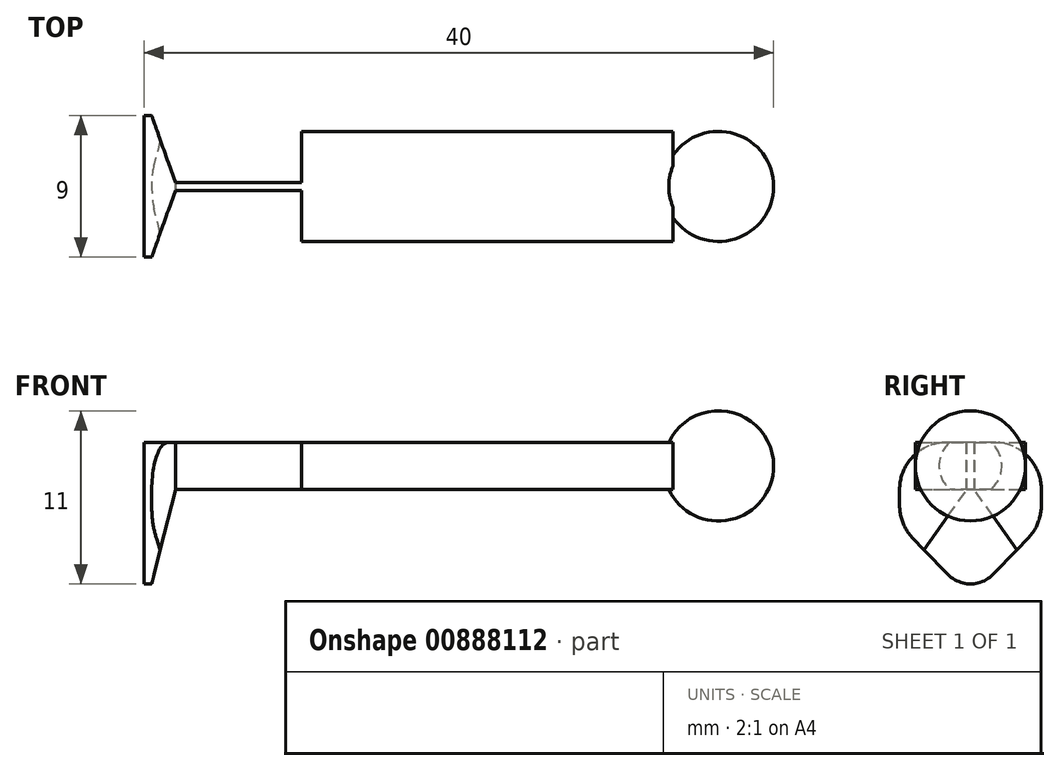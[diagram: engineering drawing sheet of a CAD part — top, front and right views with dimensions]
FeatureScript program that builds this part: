
annotation { "Feature Type Name" : "Feature", "Feature Type Description" : "" }
export const myFeature = defineFeature(function(context is Context, id is Id, definition is map)
    precondition{}
    {
        {
            var Q0;
            Q0=qCreatedBy(makeId("Front.planeOp"),FACE);
            var sketch = newSketch(context, id + "F0", { "sketchPlane" : qUnion([Q0])});
            skLineSegment(sketch, "E0", {"start": v(0, 0) * mm, "end": v(-40, 0) * mm, "construction": true});
            skArc(sketch, "E1", {"start": v(0, 0) * mm, "mid": v(-3.5, 3.5) * mm, "end": v(-7, 0) * mm});
            skLineSegment(sketch, "E2", {"start": v(-7, 0) * mm, "end": v(0, 0) * mm});
            skSolve(sketch);
        }
        {
            var Q0;
            Q0=makeQuery(id+"F0.imprint","IMPRINT",FACE,{"disambiguationData":[TD([[makeQuery(id+"F0.imprint","IMPRINT",EDGE,{"derivedFrom":sQuery(id+"F0.wireOp",EDGE,"E1")}),1.0]])]});
            var Q1;
            Q1=sQuery(id+"F0.wireOp",EDGE,"E2");
            revolve(context, id + "F1", {"surfaceOperationType" : NewSurfaceOperationType.NEW, "entities" : qUnion([Q0]), "axis" : qUnion([Q1]), "revolveType" : RevolveType.FULL});
        }
        {
            var Q0;
            Q0=qCreatedBy(makeId("Front.planeOp"),FACE);
            var sketch = newSketch(context, id + "F2", { "sketchPlane" : qUnion([Q0])});
            skLineSegment(sketch, "E3.bottom", {"start": v(-30, 1.5) * mm, "end": v(-6.38, 1.5) * mm});
            skLineSegment(sketch, "E3.top", {"start": v(-30, -1.5) * mm, "end": v(-6.38, -1.5) * mm});
            skLineSegment(sketch, "E3.left", {"start": v(-30, 1.5) * mm, "end": v(-30, -1.5) * mm});
            skLineSegment(sketch, "E3.right", {"start": v(-6.38, 1.5) * mm, "end": v(-6.38, -1.5) * mm});
            skSolve(sketch);
        }
        {
            var Q0;
            Q0=makeQuery(id+"F2.imprint","IMPRINT",FACE,{"disambiguationData":[TD([[makeQuery(id+"F2.imprint","IMPRINT",EDGE,{"derivedFrom":sQuery(id+"F2.wireOp",EDGE,"E3.bottom")}),-1.0]])]});
            extrude(context, id + "F3", {"entities" : qUnion([Q0]), "operationType" : NewBodyOperationType.ADD, "endBound" : BoundingType.SYMMETRIC, "depth" : 7 * mm, "offsetDistance" : 25 * mm});
        }
        {
            var Q0;
            Q0=qCreatedBy(makeId("Right.planeOp"),FACE);
            cPlane(context, id + "F4", {"entities" : qUnion([Q0]), "cplaneType" : CPlaneType.OFFSET, "offset" : 40 * mm, "oppositeDirection" : true, "width" : 150 * mm, "height" : 150 * mm});
        }
        {
            var Q0;
            Q0=qCreatedBy(id+"F4.planeOp",FACE);
            var sketch = newSketch(context, id + "F5", { "sketchPlane" : qUnion([Q0])});
            skLineSegment(sketch, "E4.top", {"start": v(1.5, 1.5) * mm, "end": v(-1.5, 1.5) * mm});
            skLineSegment(sketch, "E4.left", {"start": v(4.5, -2.52) * mm, "end": v(4.5, -1.5) * mm});
            skPoint(sketch, "E4.middle", {"position": v(0, -3) * mm});
            skPoint(sketch, "E5.visualSharp", {"position": v(4.5, 1.5) * mm});
            skArc(sketch, "E5.filletArc", {"start": v(4.5, -1.5) * mm, "mid": v(3.62, 0.62) * mm, "end": v(1.5, 1.5) * mm});
            skPoint(sketch, "E6.visualSharp", {"position": v(-4.5, 1.5) * mm});
            skArc(sketch, "E6.filletArc", {"start": v(-1.5, 1.5) * mm, "mid": v(-3.62, 0.62) * mm, "end": v(-4.5, -1.5) * mm});
            skLineSegment(sketch, "E7", {"start": v(1.43, -6.9) * mm, "end": v(3.65, -4.61) * mm});
            skArc(sketch, "E8.filletArc", {"start": v(3.65, -4.61) * mm, "mid": v(4.28, -3.65) * mm, "end": v(4.5, -2.52) * mm});
            skLineSegment(sketch, "E9.MirrorCS", {"start": v(-1.43, -6.9) * mm, "end": v(-3.65, -4.61) * mm});
            skArc(sketch, "E10.MirrorCS", {"start": v(-3.65, -4.61) * mm, "mid": v(-4.28, -3.65) * mm, "end": v(-4.5, -2.52) * mm});
            skPoint(sketch, "E11.visualSharp", {"position": v(0, -8.37) * mm});
            skArc(sketch, "E11.filletArc", {"start": v(-1.43, -6.9) * mm, "mid": v(0, -7.5) * mm, "end": v(1.43, -6.9) * mm});
            skPoint(sketch, "E12.visualSharp", {"position": v(-4.5, -7.5) * mm});
            skLineSegment(sketch, "E13.MirrorCS", {"start": v(-4.5, -2.52) * mm, "end": v(-4.5, -1.5) * mm});
            skSolve(sketch);
        }
        {
            var Q0;
            Q0=makeQuery(id+"F5.imprint","IMPRINT",FACE,{"disambiguationData":[TD([[makeQuery(id+"F5.imprint","IMPRINT",EDGE,{"derivedFrom":sQuery(id+"F5.wireOp",EDGE,"E4.top")}),1.0]])]});
            extrude(context, id + "F6", {"entities" : qUnion([Q0]), "depth" : 2 * mm, "offsetDistance" : 25 * mm});
        }
        {
            var Q0;
            Q0=makeQuery(id+"F6.opExtrude","CAP_FACE",FACE,{"disambiguationData":[OSD([sQuery(id+"F5.wireOp",EDGE,"E4.bottom"),sQuery(id+"F5.wireOp",EDGE,"E4.top"),sQuery(id+"F5.wireOp",EDGE,"E4.left"),sQuery(id+"F5.wireOp",EDGE,"E4.right")])],"isStart":false});
            var sketch = newSketch(context, id + "F7", { "sketchPlane" : qUnion([Q0])});
            skLineSegment(sketch, "E14.bottom", {"start": v(-0.25, 1.5) * mm, "end": v(0.25, 1.5) * mm});
            skLineSegment(sketch, "E14.top", {"start": v(-0.25, -1.5) * mm, "end": v(0.25, -1.5) * mm});
            skLineSegment(sketch, "E14.left", {"start": v(-0.25, 1.5) * mm, "end": v(-0.25, -1.5) * mm});
            skLineSegment(sketch, "E14.right", {"start": v(0.25, 1.5) * mm, "end": v(0.25, -1.5) * mm});
            skSolve(sketch);
        }
        {
            var Q0;
            Q0=makeQuery(id+"F7.imprint","IMPRINT",FACE,{"disambiguationData":[TD([[makeQuery(id+"F7.imprint","IMPRINT",EDGE,{"derivedFrom":sQuery(id+"F7.wireOp",EDGE,"E14.bottom")}),1.0]])]});
            extrude(context, id + "F8", {"entities" : qUnion([Q0]), "endBound" : BoundingType.UP_TO_NEXT, "depth" : 25 * mm, "offsetDistance" : 25 * mm});
        }
        {
            var Q0;
            Q0=makeQuery(id+"F6.opExtrude","SWEPT_BODY",BODY,{"disambiguationData":[OSD([sQuery(id+"F5.wireOp",EDGE,"E4.top"),sQuery(id+"F5.wireOp",EDGE,"E4.left"),sQuery(id+"F5.wireOp",EDGE,"E5.filletArc"),sQuery(id+"F5.wireOp",EDGE,"E6.filletArc"),sQuery(id+"F5.wireOp",EDGE,"E7"),sQuery(id+"F5.wireOp",EDGE,"E8.filletArc"),sQuery(id+"F5.wireOp",EDGE,"E9.MirrorCS"),sQuery(id+"F5.wireOp",EDGE,"E10.MirrorCS"),sQuery(id+"F5.wireOp",EDGE,"E11.filletArc"),sQuery(id+"F5.wireOp",EDGE,"E13.MirrorCS")])]});
            var Q1;
            Q1=makeQuery(id+"F8.opExtrude","SWEPT_BODY",BODY,{"disambiguationData":[OSD([sQuery(id+"F7.wireOp",EDGE,"E14.bottom"),sQuery(id+"F7.wireOp",EDGE,"E14.top"),sQuery(id+"F7.wireOp",EDGE,"E14.left"),sQuery(id+"F7.wireOp",EDGE,"E14.right")])]});
            booleanBodies(context, id + "F9", {"operationType" : BooleanOperationType.UNION, "tools" : qUnion([Q0, Q1])});
        }
        {
            var Q0;
            Q0=makeQuery(id+"F1.opRevolve","SWEPT_BODY",BODY,{"disambiguationData":[OSD([sQuery(id+"F0.wireOp",EDGE,"E1"),sQuery(id+"F0.wireOp",EDGE,"E2")])]});
            var Q1;
            Q1=makeQuery(id+"F6.opExtrude","SWEPT_BODY",BODY,{"disambiguationData":[OSD([sQuery(id+"F5.wireOp",EDGE,"E4.top"),sQuery(id+"F5.wireOp",EDGE,"E4.left"),sQuery(id+"F5.wireOp",EDGE,"E5.filletArc"),sQuery(id+"F5.wireOp",EDGE,"E6.filletArc"),sQuery(id+"F5.wireOp",EDGE,"E7"),sQuery(id+"F5.wireOp",EDGE,"E8.filletArc"),sQuery(id+"F5.wireOp",EDGE,"E9.MirrorCS"),sQuery(id+"F5.wireOp",EDGE,"E10.MirrorCS"),sQuery(id+"F5.wireOp",EDGE,"E11.filletArc"),sQuery(id+"F5.wireOp",EDGE,"E13.MirrorCS")])]});
            booleanBodies(context, id + "F10", {"operationType" : BooleanOperationType.UNION, "tools" : qUnion([Q0, Q1])});
        }
        {
            var Q0;
            Q0=qCreatedBy(makeId("Top.planeOp"),FACE);
            var sketch = newSketch(context, id + "F11", { "sketchPlane" : qUnion([Q0])});
            skLineSegment(sketch, "E15", {"start": v(-38, 0.25) * mm, "end": v(-39.5, 4.5) * mm});
            skLineSegment(sketch, "E16", {"start": v(-38, 4.5) * mm, "end": v(-38, 0.25) * mm});
            skLineSegment(sketch, "E17.MirrorCS", {"start": v(-38, -0.25) * mm, "end": v(-39.5, -4.5) * mm});
            skLineSegment(sketch, "E18.MirrorCS", {"start": v(-38, -4.5) * mm, "end": v(-38, -0.25) * mm});
            skLineSegment(sketch, "E19", {"start": v(-39.5, 4.5) * mm, "end": v(-38, 4.5) * mm});
            skLineSegment(sketch, "E20.MirrorCS", {"start": v(-39.5, -4.5) * mm, "end": v(-38, -4.5) * mm});
            skSolve(sketch);
        }
        {
            var Q0;
            Q0=makeQuery(id+"F11.imprint","IMPRINT",FACE,{"disambiguationData":[TD([[makeQuery(id+"F11.imprint","IMPRINT",EDGE,{"derivedFrom":sQuery(id+"F11.wireOp",EDGE,"E15")}),-1.0]])]});
            var Q1;
            Q1=makeQuery(id+"F11.imprint","IMPRINT",FACE,{"disambiguationData":[TD([[makeQuery(id+"F11.imprint","IMPRINT",EDGE,{"derivedFrom":sQuery(id+"F11.wireOp",EDGE,"E17.MirrorCS")}),1.0]])]});
            extrude(context, id + "F12", {"entities" : qUnion([Q0, Q1]), "operationType" : NewBodyOperationType.REMOVE, "endBound" : BoundingType.SYMMETRIC, "oppositeDirection" : true, "depth" : 30 * mm, "offsetDistance" : 25 * mm});
        }
        {
            var Q0;
            Q0=qCreatedBy(makeId("Front.planeOp"),FACE);
            var sketch = newSketch(context, id + "F13", { "sketchPlane" : qUnion([Q0])});
            skLineSegment(sketch, "E21", {"start": v(-38, -1.5) * mm, "end": v(-39.5, -7.5) * mm});
            skLineSegment(sketch, "E22", {"start": v(-39.5, -7.5) * mm, "end": v(-38, -7.5) * mm});
            skLineSegment(sketch, "E23", {"start": v(-38, -7.5) * mm, "end": v(-38, -1.5) * mm});
            skSolve(sketch);
        }
        {
            var Q0;
            Q0=makeQuery(id+"F13.imprint","IMPRINT",FACE,{"disambiguationData":[TD([[makeQuery(id+"F13.imprint","IMPRINT",EDGE,{"derivedFrom":sQuery(id+"F13.wireOp",EDGE,"E21")}),1.0]])]});
            extrude(context, id + "F14", {"entities" : qUnion([Q0]), "operationType" : NewBodyOperationType.REMOVE, "endBound" : BoundingType.SYMMETRIC, "oppositeDirection" : true, "depth" : 30 * mm, "offsetDistance" : 25 * mm});
        }
    });
